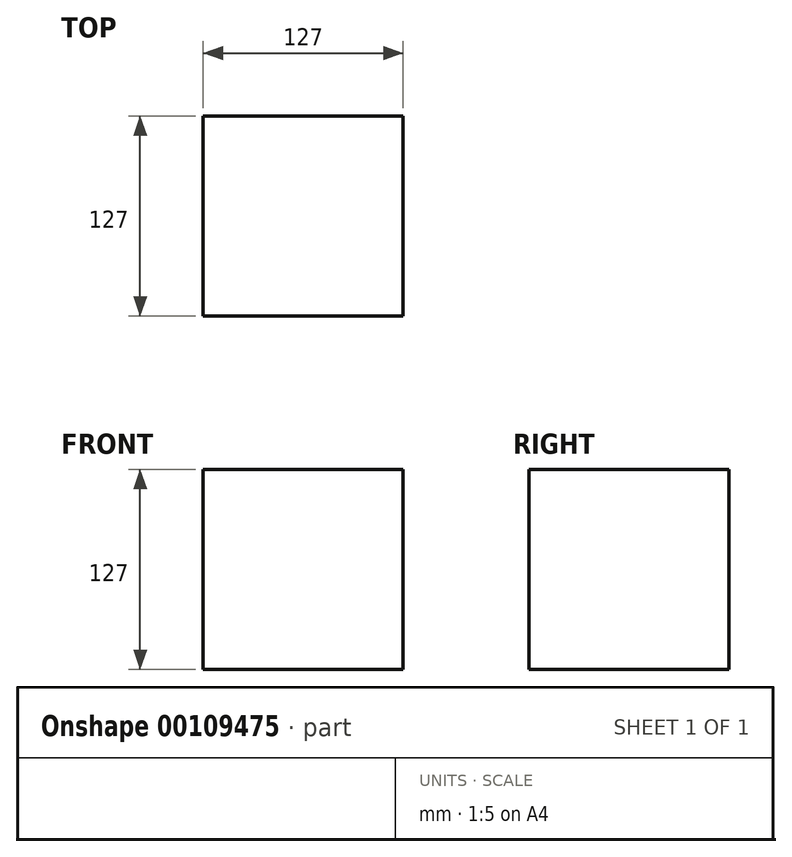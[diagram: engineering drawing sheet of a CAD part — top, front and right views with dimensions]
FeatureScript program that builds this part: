
annotation { "Feature Type Name" : "Feature", "Feature Type Description" : "" }
export const myFeature = defineFeature(function(context is Context, id is Id, definition is map)
    precondition{}
    {
        {
            var Q0;
            Q0=qCreatedBy(makeId("Top.planeOp"),FACE);
            var sketch = newSketch(context, id + "F0", { "sketchPlane" : qUnion([Q0])});
            skLineSegment(sketch, "E0.bottom", {"start": v(-40.98, 68.88) * mm, "end": v(86.02, 68.88) * mm});
            skLineSegment(sketch, "E0.top", {"start": v(-40.98, -58.12) * mm, "end": v(86.02, -58.12) * mm});
            skLineSegment(sketch, "E0.left", {"start": v(-40.98, 68.88) * mm, "end": v(-40.98, -58.12) * mm});
            skLineSegment(sketch, "E0.right", {"start": v(86.02, 68.88) * mm, "end": v(86.02, -58.12) * mm});
            skSolve(sketch);
        }
        {
            var Q0;
            Q0=makeQuery(id+"F0.imprint","IMPRINT",FACE,{"disambiguationData":[TD([[makeQuery(id+"F0.imprint","IMPRINT",EDGE,{"derivedFrom":sQuery(id+"F0.wireOp",EDGE,"E0.bottom")}),-1.0]])]});
            extrude(context, id + "F1", {"entities" : qUnion([Q0]), "endBound" : BoundingType.SYMMETRIC, "depth" : 127 * mm});
        }
    });
